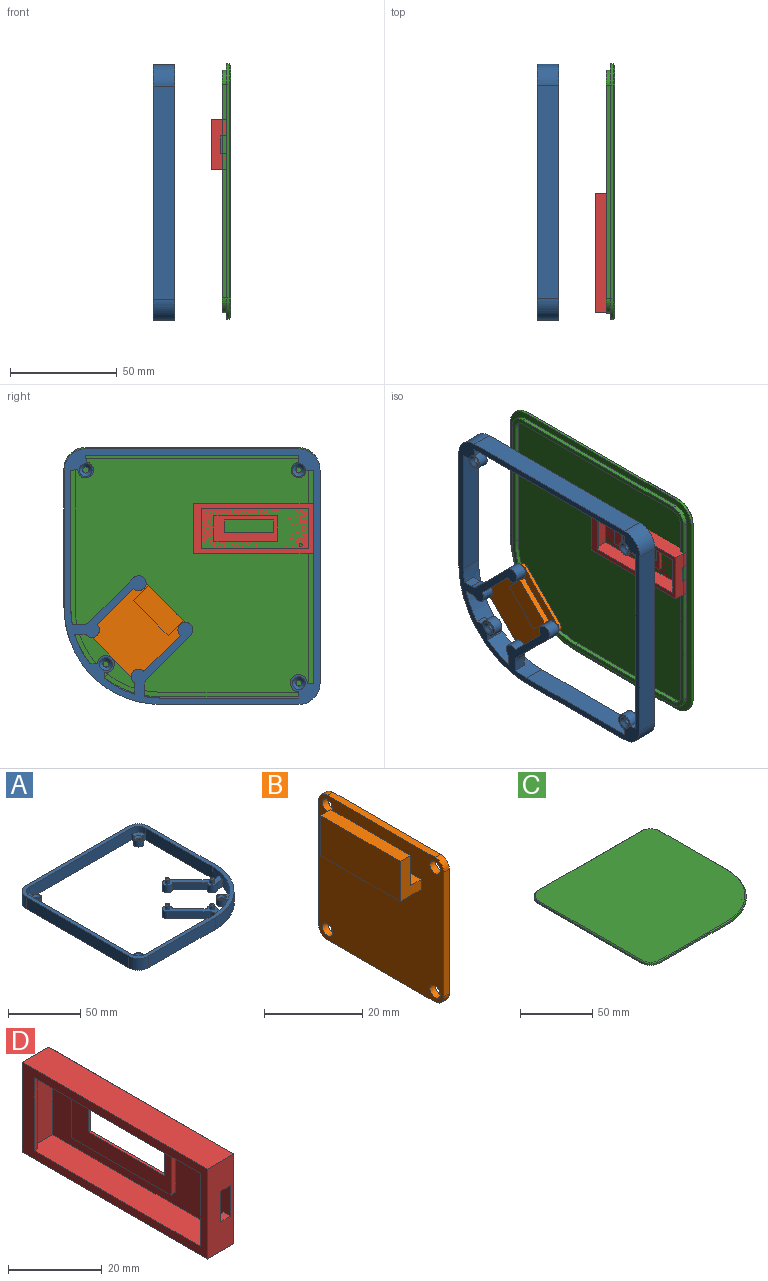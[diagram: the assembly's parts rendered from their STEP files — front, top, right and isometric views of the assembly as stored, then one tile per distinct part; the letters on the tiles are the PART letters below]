
ASSEMBLY  parts=4 mates=2
PART A: 82 faces, bbox 120x120x10 mm
  f0: plane 65x10mm, normal (1,0,0), area 650mm2, adj f1,f15,f16,f69
  f1: cylinder r=10mm len=10mm, axis (0,0,-1), area 157.1mm2, adj f0,f2,f16,f69
  f2: plane 100x10mm, normal (0,1,0), area 1000mm2, adj f1,f3,f16,f69
  f3: cylinder r=10mm len=10mm, axis (0,0,-1), area 157.1mm2, adj f2,f4,f16,f69
  f4: plane 100x10mm, normal (-1,0,0), area 1000mm2, adj f3,f5,f16,f69
  f5: cylinder r=10mm len=10mm, axis (0,0,-1), area 157.1mm2, adj f4,f6,f16,f69
  f6: plane 65x10mm, normal (0,-1,0), area 650mm2, adj f5,f15,f16,f69
  f7: plane 10x3mm, normal (-1,0,0), area 15.2mm2, adj f8,f14,f16,f22,f23,f69
  f8: cylinder r=7.05mm len=10mm, axis (0,0,-1), area 0.7mm2, adj f7,f9,f16,f69
  f9: cylinder r=42mm len=25.92mm, axis (0,0,-1), area 251mm2, adj f8,f10,f16,f56,f57,f60,f69
  f10: plane 65x10mm, normal (0,1,0), area 650mm2, adj f9,f16,f18,f50,f69
  f11: plane 100x10mm, normal (1,0,0), area 1000mm2, adj f16,f17,f24,f50,f51,f69
  f12: plane 100x10mm, normal (0,-1,0), area 1000mm2, adj f16,f26,f28,f51,f52,f69
  f13: plane 65x10mm, normal (-1,0,0), area 650mm2, adj f14,f16,f30,f52,f69
  f14: cylinder r=42mm len=32.99mm, axis (0,0,-1), area 300.8mm2, adj f7,f13,f16,f21,f23,f61,f62,f68
  f15: cylinder r=45mm len=45mm, axis (0,0,-1), area 706.9mm2, adj f0,f6,f16,f69
  f16: plane 120x120mm, normal (0,0,-1), area 1867.2mm2, adj f0,f1,f2,f3,f4,f5,f6,f7
  f17: plane 5x3mm, normal (0,1,0), area 15mm2, adj f11,f16,f19,f20
  f18: plane 5x3mm, normal (1,0,0), area 15mm2, adj f10,f16,f19,f20
  f19: cylinder r=4mm len=8mm, axis (0,0,-1), area 94.2mm2, adj f16,f17,f18,f20
  f20: plane 11x11mm, normal (0,0,1), area 47.9mm2, adj f17,f18,f19,f39,f50
  f21: plane 5x3.56mm, normal (0,1,0), area 17.8mm2, adj f14,f16,f22,f23
  f22: cylinder r=4mm len=8mm, axis (0,0,-1), area 96mm2, adj f7,f16,f21,f23
  f23: plane 11.55x10.91mm, normal (0,0,1), area 37.8mm2, adj f7,f14,f21,f22,f34
  f24: plane 5x3.5mm, normal (0,-1,0), area 17.5mm2, adj f11,f16,f25,f27
  f25: cylinder r=3.5mm len=7mm, axis (0,0,-1), area 82.5mm2, adj f16,f24,f26,f27
  f26: plane 5x3.5mm, normal (1,0,0), area 17.5mm2, adj f12,f16,f25,f27
  f27: plane 10.5x10.5mm, normal (0,0,1), area 39.1mm2, adj f24,f25,f26,f40,f51
  f28: plane 5x3.32mm, normal (-1,0.09,0), area 16.7mm2, adj f12,f16,f29,f32
  f29: cylinder r=3.69mm len=7.38mm, axis (0,0,-1), area 85.7mm2, adj f16,f28,f30,f32
  f30: plane 5x3.31mm, normal (-0.02,-1,0), area 16.6mm2, adj f13,f16,f29,f32
  f31: cylinder r=1.5mm len=3mm, axis (0,0,-1), area 18.8mm2, adj f35,f38
  f32: plane 10.69x10.69mm, normal (0,0,1), area 42.7mm2, adj f28,f29,f30,f38,f52
  f33: cone r=3mm half-angle=45deg, axis (0,0,-1), area 30mm2, adj f16,f48
  f34: cone r=1.5mm half-angle=45deg, axis (0,0,1), area 30mm2, adj f23,f47
  f35: cone r=3mm half-angle=45deg, axis (0,0,-1), area 30mm2, adj f16,f31
  f36: cone r=3mm half-angle=45deg, axis (0,0,-1), area 30mm2, adj f16,f42
  f37: cone r=3mm half-angle=45deg, axis (0,0,-1), area 30mm2, adj f16,f44
  f38: cone r=1.5mm half-angle=45deg, axis (0,0,1), area 30mm2, adj f31,f32
  f39: cone r=1.5mm half-angle=45deg, axis (0,0,1), area 30mm2, adj f20,f41
  f40: cone r=1.5mm half-angle=45deg, axis (0,0,1), area 30mm2, adj f27,f45
  f41: plane 3x3mm, normal (0,0,1), area 1.8mm2, adj f39,f43
  f42: plane 3x3mm, normal (0,0,-1), area 1.8mm2, adj f36,f43
  f43: cylinder r=1.3mm len=2.6mm, axis (0,0,-1), area 16.3mm2, adj f41,f42
  f44: plane 3x3mm, normal (0,0,-1), area 1.8mm2, adj f37,f46
  f45: plane 3x3mm, normal (0,0,1), area 1.8mm2, adj f40,f46
  f46: cylinder r=1.3mm len=2.6mm, axis (0,0,-1), area 16.3mm2, adj f44,f45
  f47: plane 3x3mm, normal (0,0,1), area 1.8mm2, adj f34,f49
  f48: plane 3x3mm, normal (0,0,-1), area 1.8mm2, adj f33,f49
  f49: cylinder r=1.3mm len=2.6mm, axis (0,0,-1), area 16.3mm2, adj f47,f48
  f50: cylinder r=7mm len=7mm, axis (0,0,-1), area 55mm2, adj f10,f11,f20,f69
  f51: cylinder r=7mm len=7mm, axis (0,0,-1), area 55mm2, adj f11,f12,f27,f69
  f52: cylinder r=7mm len=7mm, axis (0,0,-1), area 55mm2, adj f12,f13,f32,f69
  f53: cylinder r=3.5mm len=7mm, axis (0,0,-1), area 99mm2, adj f16,f54,f59,f60
  f54: plane 20.46x20.46mm, normal (-0.71,-0.71,0), area 173.6mm2, adj f16,f53,f55,f60
  f55: cylinder r=5mm len=6mm, axis (0,0,-1), area 23.8mm2, adj f16,f54,f56,f60
  f56: plane 6x4.76mm, normal (-1,0,0), area 28.5mm2, adj f9,f16,f55,f60
  f57: plane 6x5.4mm, normal (1,0,0), area 32.4mm2, adj f9,f16,f58,f60
  f58: cylinder r=3.51mm len=6.35mm, axis (0,0,-1), area 69.5mm2, adj f16,f57,f59,f60
  f59: plane 16.97x16.97mm, normal (0.71,0.71,0), area 144mm2, adj f16,f53,f58,f60
  f60: plane 34.79x28.94mm, normal (0,0,1), area 178.5mm2, adj f9,f53,f54,f55,f56,f57,f58,f59
  f61: plane 6x5.4mm, normal (0,-1,0), area 32.4mm2, adj f14,f16,f67,f68
  f62: plane 6x4.72mm, normal (0,1,0), area 28.3mm2, adj f14,f16,f63,f68
  f63: cylinder r=5mm len=6mm, axis (0,0,-1), area 23.6mm2, adj f16,f62,f64,f68
  f64: plane 20.46x20.46mm, normal (0.71,0.71,0), area 173.6mm2, adj f16,f63,f65,f68
  f65: cylinder r=3.49mm len=6.98mm, axis (0,0,-1), area 98.7mm2, adj f16,f64,f66,f68
  f66: plane 16.99x16.99mm, normal (-0.71,-0.71,0), area 144.2mm2, adj f16,f65,f67,f68
  f67: cylinder r=3.49mm len=6.22mm, axis (0,0,-1), area 68.2mm2, adj f16,f61,f66,f68
  f68: plane 34.68x28.91mm, normal (0,0,1), area 177.9mm2, adj f14,f61,f62,f63,f64,f65,f66,f67
  f69: plane 120x120mm, normal (0,0,1), area 1315.2mm2, adj f0,f1,f2,f3,f4,f5,f6,f7
  f70: cylinder r=1.49mm len=3mm, axis (0,0,-1), area 28.1mm2, adj f68,f72
  f71: plane 0.98x0.98mm, normal (0,0,1), area 0.8mm2, adj f72
  f72: torus R=0.49mm, axis (0,0,1), area 11.1mm2, adj f70,f71
  f73: cylinder r=1.49mm len=3mm, axis (0,0,-1), area 28.1mm2, adj f68,f75
  f74: plane 0.98x0.98mm, normal (0,0,1), area 0.8mm2, adj f75
  f75: torus R=0.49mm, axis (0,0,1), area 11.1mm2, adj f73,f74
  f76: cylinder r=1.5mm len=3mm, axis (0,0,-1), area 28.3mm2, adj f60,f78
  f77: plane 1x1mm, normal (0,0,1), area 0.8mm2, adj f78
  f78: torus R=0.5mm, axis (0,0,1), area 11.2mm2, adj f76,f77
  f79: cylinder r=1.51mm len=3.02mm, axis (0,0,-1), area 28.5mm2, adj f60,f81
  f80: plane 1.02x1.02mm, normal (0,0,1), area 0.8mm2, adj f81
  f81: torus R=0.51mm, axis (0,0,1), area 11.3mm2, adj f79,f80
PART B: 21 faces, bbox 7.6x36x36 mm
  f0: plane 23x3mm, normal (0,0,1), area 69mm2, adj f1,f15,f17,f20
  f1: plane 36x36mm, normal (-1,0,0), area 1204.9mm2, adj f0,f2,f3,f4,f5,f6,f7,f8
  f2: plane 31x1.6mm, normal (0,-1,0), area 49.6mm2, adj f1,f10,f13,f14
  f3: plane 31x1.6mm, normal (0,0,-1), area 49.6mm2, adj f1,f10,f11,f14
  f4: plane 31x1.6mm, normal (0,1,0), area 49.6mm2, adj f1,f10,f11,f12
  f5: cylinder r=1.5mm len=3mm, axis (-1,0,0), area 15.1mm2, adj f1,f10
  f6: cylinder r=1.5mm len=3mm, axis (-1,0,0), area 15.1mm2, adj f1,f10
  f7: cylinder r=1.5mm len=3mm, axis (-1,0,0), area 15.1mm2, adj f1,f10
  f8: plane 31x1.6mm, normal (0,0,1), area 49.6mm2, adj f1,f10,f12,f13
  f9: cylinder r=1.5mm len=3mm, axis (-1,0,0), area 15.1mm2, adj f1,f10
  f10: plane 36x36mm, normal (1,0,0), area 1262.4mm2, adj f2,f3,f4,f5,f6,f7,f8,f9
  f11: cylinder r=2.5mm len=2.5mm, axis (1,0,0), area 6.3mm2, adj f1,f3,f4,f10
  f12: cylinder r=2.5mm len=2.5mm, axis (-1,0,0), area 6.3mm2, adj f1,f4,f8,f10
  f13: cylinder r=2.5mm len=2.5mm, axis (1,0,0), area 6.3mm2, adj f1,f2,f8,f10
  f14: cylinder r=2.5mm len=2.5mm, axis (-1,0,0), area 6.3mm2, adj f1,f2,f3,f10
  f15: plane 10x6mm, normal (0,-1,0), area 37.5mm2, adj f0,f1,f16,f18,f19,f20
  f16: plane 23x6mm, normal (0,0,-1), area 138mm2, adj f1,f15,f17,f18
  f17: plane 10x6mm, normal (0,1,0), area 37.5mm2, adj f0,f1,f16,f18,f19,f20
  f18: plane 23x10mm, normal (-1,0,0), area 230mm2, adj f15,f16,f17,f19
  f19: plane 23x3mm, normal (0,0,1), area 69mm2, adj f15,f17,f18,f20
  f20: plane 23x7.5mm, normal (1,0,0), area 172.5mm2, adj f0,f15,f17,f19
PART C: 42 faces, bbox 120x120x4 mm
  f0: plane 65x1.25mm, normal (1,0,0), area 81.2mm2, adj f1,f9,f12,f36
  f1: cylinder r=10mm len=10mm, axis (0,0,-1), area 19.6mm2, adj f0,f2,f12,f34
  f2: plane 100x1.25mm, normal (0,1,0), area 125mm2, adj f1,f3,f12,f35
  f3: cylinder r=10mm len=10mm, axis (0,0,-1), area 19.6mm2, adj f2,f4,f12,f37
  f4: plane 100x1.25mm, normal (-1,0,0), area 125mm2, adj f3,f5,f12,f39
  f5: cylinder r=10mm len=10mm, axis (0,0,-1), area 19.6mm2, adj f4,f6,f12,f41
  f6: plane 65x1.25mm, normal (0,-1,0), area 81.2mm2, adj f5,f9,f12,f40
  f7: plane 2x0.05mm, normal (-1,0,0), area 0.1mm2, adj f8,f10,f11,f12
  f8: cylinder r=7.05mm len=2mm, axis (0,0,-1), area 0.1mm2, adj f7,f10,f11,f12
  f9: cylinder r=45mm len=45mm, axis (0,0,-1), area 88.4mm2, adj f0,f6,f12,f38
  f10: cylinder r=42mm len=2mm, axis (0,0,-1), area 0.2mm2, adj f7,f8,f11,f12
  f11: plane 118.5x118.5mm, normal (0,0,1), area 13567mm2, adj f7,f8,f10,f34,f35,f36,f37,f38
  f12: plane 120x120mm, normal (0,0,-1), area 13015.6mm2, adj f0,f1,f2,f3,f4,f5,f6,f7
  f13: plane 2x1.65mm, normal (0.79,0.62,0), area 4.2mm2, adj f12,f14,f19,f27
  f14: plane 113.8x113.8mm, normal (0,0,-1), area 885.5mm2, adj f13,f15,f16,f17,f18,f19,f20,f21
  f15: plane 2x1.65mm, normal (-0.79,-0.62,0), area 4.2mm2, adj f12,f14,f18,f28
  f16: cylinder r=4.8mm len=4.8mm, axis (0,0,-1), area 15.1mm2, adj f12,f14,f17,f24
  f17: plane 65x2mm, normal (-1,0,0), area 130mm2, adj f12,f14,f16,f18
  f18: cylinder r=39.8mm len=31.26mm, axis (0,0,-1), area 71.9mm2, adj f12,f14,f15,f17
  f19: cylinder r=39.8mm len=24.57mm, axis (0,0,-1), area 53mm2, adj f12,f13,f14,f20
  f20: plane 65x2mm, normal (0,1,0), area 130mm2, adj f12,f14,f19,f21
  f21: cylinder r=4.8mm len=4.8mm, axis (0,0,-1), area 15.1mm2, adj f12,f14,f20,f22
  f22: plane 100x2mm, normal (1,0,0), area 200mm2, adj f12,f14,f21,f23
  f23: cylinder r=4.8mm len=4.8mm, axis (0,0,-1), area 15.1mm2, adj f12,f14,f22,f24
  f24: plane 100x2mm, normal (0,-1,0), area 200mm2, adj f12,f14,f16,f23
  f25: cylinder r=6.9mm len=6.9mm, axis (0,0,-1), area 21.7mm2, adj f12,f14,f26,f32
  f26: plane 65x2mm, normal (0,-1,0), area 130mm2, adj f12,f14,f25,f27
  f27: cylinder r=41.9mm len=25.86mm, axis (0,0,-1), area 55.7mm2, adj f12,f13,f14,f26
  f28: cylinder r=41.9mm len=32.91mm, axis (0,0,-1), area 75.7mm2, adj f12,f14,f15,f29
  f29: plane 65x2mm, normal (1,0,0), area 130mm2, adj f12,f14,f28,f30
  f30: cylinder r=6.9mm len=6.9mm, axis (0,0,-1), area 21.7mm2, adj f12,f14,f29,f31
  f31: plane 100x2mm, normal (0,1,0), area 200mm2, adj f12,f14,f30,f33
  f32: plane 100x2mm, normal (-1,0,0), area 200mm2, adj f12,f14,f25,f33
  f33: cylinder r=6.9mm len=6.9mm, axis (0,0,-1), area 21.7mm2, adj f12,f14,f31,f32
  f34: cone r=9.25mm half-angle=45deg, axis (0,0,-1), area 16mm2, adj f1,f11,f35,f36
  f35: plane 100x0.75mm, normal (0,0.71,0.71), area 106.1mm2, adj f2,f11,f34,f37
  f36: plane 65x0.75mm, normal (0.71,0,0.71), area 68.9mm2, adj f0,f11,f34,f38
  f37: cone r=9.25mm half-angle=45deg, axis (0,0,-1), area 16mm2, adj f3,f11,f35,f39
  f38: cone r=44.25mm half-angle=45deg, axis (0,0,-1), area 74.3mm2, adj f9,f11,f36,f40
  f39: plane 100x0.75mm, normal (-0.71,0,0.71), area 106.1mm2, adj f4,f11,f37,f41
  f40: plane 65x0.75mm, normal (0,-0.71,0.71), area 68.9mm2, adj f6,f11,f38,f41
  f41: cone r=9.25mm half-angle=45deg, axis (0,0,-1), area 16mm2, adj f5,f11,f39,f40
PART D: 35 faces, bbox 9x56x23.5 mm
  f0: plane 19.1x1mm, normal (0,-1,0), area 19.1mm2, adj f2,f3,f5,f6
  f1: plane 19.1x0.5mm, normal (1,0,0), area 9.6mm2, adj f3,f4,f5,f6
  f2: plane 56x23.5mm, normal (-1,0,0), area 359.1mm2, adj f0,f5,f6,f7,f8,f9,f10,f31
  f3: plane 19.1x1mm, normal (0.71,-0.71,0), area 27mm2, adj f0,f1,f5,f6
  f4: plane 19.1x5mm, normal (0,-1,0), area 95.5mm2, adj f1,f5,f6,f17
  f5: plane 51.6x7mm, normal (0,0,1), area 358.7mm2, adj f0,f1,f2,f3,f4,f17,f31
  f6: plane 51.6x7mm, normal (0,0,-1), area 358.7mm2, adj f0,f1,f2,f3,f4,f17,f31
  f7: plane 23.5x8mm, normal (0,-1,0), area 164mm2, adj f2,f8,f10,f17,f30,f32,f33,f34
  f8: plane 56x8mm, normal (0,0,-1), area 448mm2, adj f2,f7,f9,f28
  f9: plane 23.5x8mm, normal (0,1,0), area 188mm2, adj f2,f8,f10,f27
  f10: plane 56x8mm, normal (0,0,1), area 448mm2, adj f2,f7,f9,f29
  f11: plane 54x21.5mm, normal (1,0,0), area 831.7mm2, adj f22,f23,f24,f25,f26,f27,f28,f29
  f12: plane 30x1.5mm, normal (0,0,-1), area 45mm2, adj f13,f15,f16,f17
  f13: plane 12x1.5mm, normal (0,1,0), area 18mm2, adj f12,f14,f16,f17
  f14: plane 30x1.5mm, normal (0,0,1), area 45mm2, adj f13,f15,f16,f17
  f15: plane 12x1.5mm, normal (0,-1,0), area 18mm2, adj f12,f14,f16,f17
  f16: plane 30x12mm, normal (-1,0,0), area 222mm2, adj f12,f13,f14,f15,f18,f19,f20,f21
  f17: plane 53.8x19.1mm, normal (-1,0,0), area 641.6mm2, adj f4,f5,f6,f7,f12,f13,f14,f15
  f18: plane 23x0.75mm, normal (0,0,1), area 17.3mm2, adj f16,f19,f21,f24
  f19: plane 6x0.75mm, normal (0,-1,0), area 4.5mm2, adj f16,f18,f20,f25
  f20: plane 23x0.75mm, normal (0,0,-1), area 17.3mm2, adj f16,f19,f21,f23
  f21: plane 6x0.75mm, normal (0,1,0), area 4.5mm2, adj f16,f18,f20,f22
  f22: plane 11.5x2.75mm, normal (0.71,0.71,0), area 34mm2, adj f11,f21,f23,f24
  f23: plane 28.5x2.75mm, normal (0.71,0,-0.71), area 100.1mm2, adj f11,f20,f22,f25
  f24: plane 28.5x2.75mm, normal (0.71,0,0.71), area 100.1mm2, adj f11,f18,f22,f25
  f25: plane 11.5x2.75mm, normal (0.71,-0.71,0), area 34mm2, adj f11,f19,f23,f24
  f26: cylinder r=0.71mm len=2mm, axis (-1,0,0), area 8.9mm2, adj f11,f17
  f27: plane 23.5x1mm, normal (0.71,0.71,0), area 31.8mm2, adj f9,f11,f28,f29
  f28: plane 56x1mm, normal (0.71,0,-0.71), area 77.8mm2, adj f8,f11,f27,f30
  f29: plane 56x1mm, normal (0.71,0,0.71), area 77.8mm2, adj f10,f11,f27,f30
  f30: plane 23.5x1mm, normal (0.71,-0.71,0), area 31.8mm2, adj f7,f11,f28,f29
  f31: plane 19.1x7mm, normal (0,1,0), area 109.7mm2, adj f2,f5,f6,f17,f32,f33,f34
  f32: plane 8x2.2mm, normal (1,0,0), area 17.6mm2, adj f7,f31,f33,f34
  f33: plane 3x2.2mm, normal (0,0,1), area 6.6mm2, adj f7,f17,f31,f32
  f34: plane 3x2.2mm, normal (0,0,-1), area 6.6mm2, adj f7,f17,f31,f32
PLACE A rot(axis=(0.58,0.58,0.58),120deg) t=(-4.7,-49.5,-22.11)mm
PLACE B rot(axis=(1,0,0),45deg) t=(-0.7,-24.37,-47.13)mm
PLACE C rot(axis=(0.58,0.58,0.58),120deg) t=(19.66,-49.3,-21.55)mm
PLACE D rot(axis=(0.03,-0.91,0.41),0deg) t=(24.66,-103.7,0.45)mm
MATE planar D.f11 <-> C.f11  axis (1,0,0) through (31.66,-90.45,1.45)mm
MATE cylindrical B.f6 <-> A.f65  axis (-1,0,0) through (2.3,-24.37,-25.21)mm
